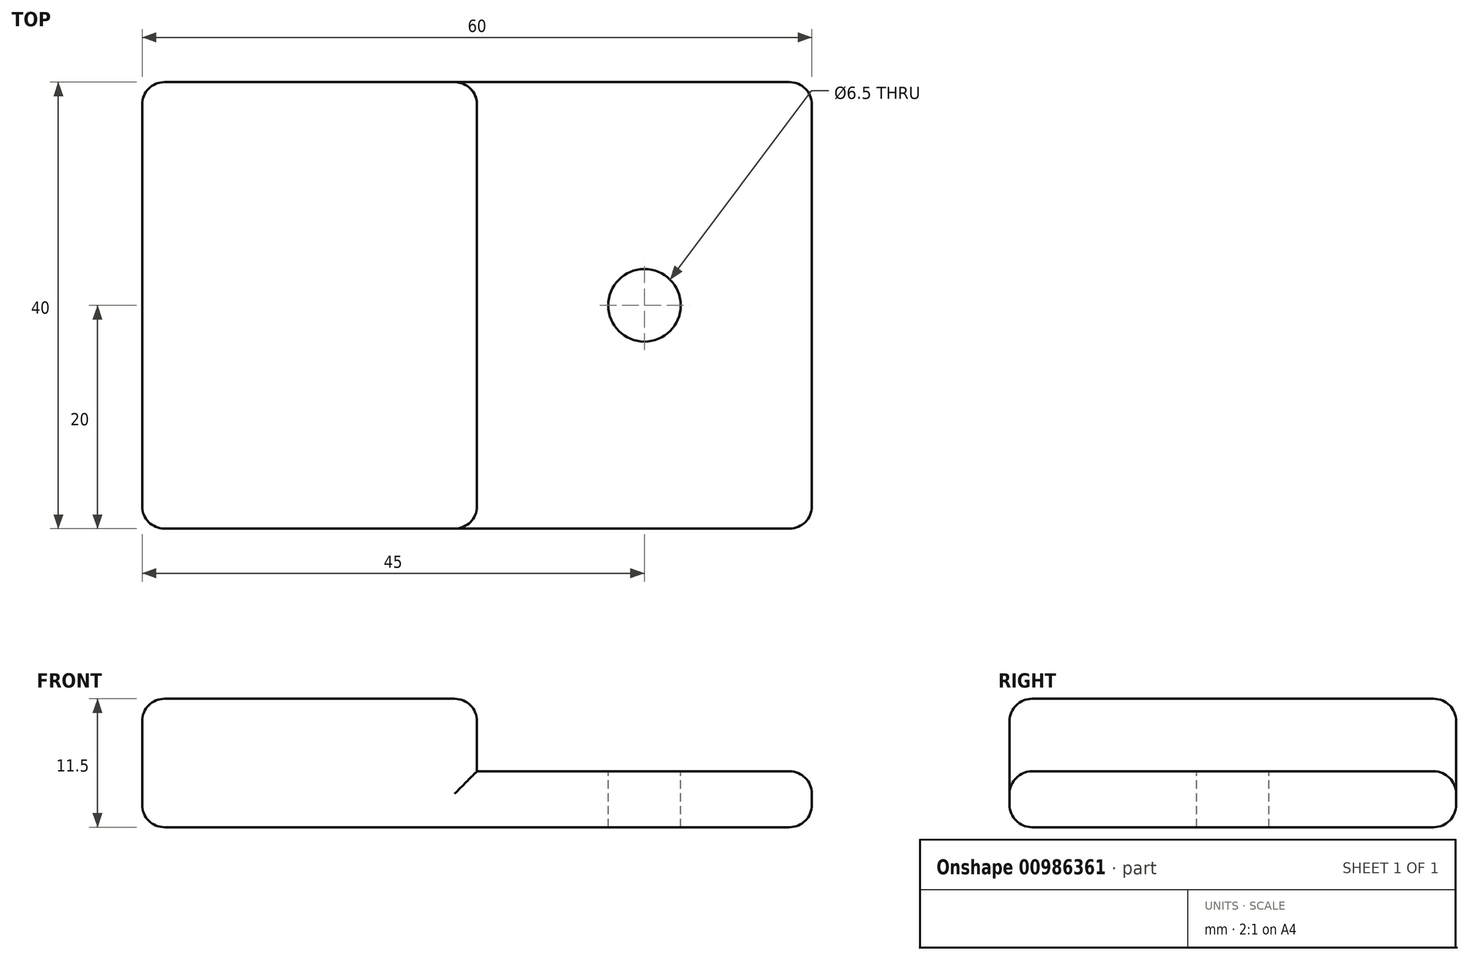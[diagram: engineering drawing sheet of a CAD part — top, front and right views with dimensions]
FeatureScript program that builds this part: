
annotation { "Feature Type Name" : "Feature", "Feature Type Description" : "" }
export const myFeature = defineFeature(function(context is Context, id is Id, definition is map)
    precondition{}
    {
        {
            var Q0;
            Q0=qCreatedBy(makeId("Front.planeOp"),FACE);
            var sketch = newSketch(context, id + "F0", { "sketchPlane" : qUnion([Q0])});
            skLineSegment(sketch, "E0", {"start": v(0, 0) * mm, "end": v(0, 11.5) * mm});
            skLineSegment(sketch, "E1", {"start": v(0, 11.5) * mm, "end": v(30, 11.5) * mm});
            skLineSegment(sketch, "E2", {"start": v(30, 11.5) * mm, "end": v(30, 5) * mm});
            skLineSegment(sketch, "E3", {"start": v(30, 5) * mm, "end": v(60, 5) * mm});
            skLineSegment(sketch, "E4", {"start": v(60, 5) * mm, "end": v(60, 0) * mm});
            skLineSegment(sketch, "E5", {"start": v(60, 0) * mm, "end": v(0, 0) * mm});
            skSolve(sketch);
        }
        {
            var Q0;
            Q0=makeQuery(id+"F0.imprint","IMPRINT",FACE,{"disambiguationData":[TD([[makeQuery(id+"F0.imprint","IMPRINT",EDGE,{"derivedFrom":sQuery(id+"F0.wireOp",EDGE,"E0")}),-1.0]])]});
            extrude(context, id + "F1", {"entities" : qUnion([Q0]), "depth" : 40 * mm, "offsetDistance" : 25 * mm});
        }
        {
            var Q0;
            Q0=makeQuery(id+"F1.opExtrude","SWEPT_FACE",FACE,{"disambiguationData":[OSD([sQuery(id+"F0.wireOp",EDGE,"E3")])]});
            var sketch = newSketch(context, id + "F2", { "sketchPlane" : qUnion([Q0])});
            skLineSegment(sketch, "E6.0", {"start": v(45, -40) * mm, "end": v(45, 0) * mm});
            skLineSegment(sketch, "E7.0", {"start": v(30, -20) * mm, "end": v(60, -20) * mm});
            skCircle(sketch, "E8", {"center": v(45, -20) * mm, "radius": 1.1 * mm});
            skSolve(sketch);
        }
        {
            var Q0;
            Q0=sQuery(id+"F2.wireOp",VERTEX,"E8.center");
            var Q1;
            Q1=makeQuery(id+"F1.opExtrude","SWEPT_BODY",BODY,{"disambiguationData":[OSD([sQuery(id+"F0.wireOp",EDGE,"E0"),sQuery(id+"F0.wireOp",EDGE,"E1"),sQuery(id+"F0.wireOp",EDGE,"E2"),sQuery(id+"F0.wireOp",EDGE,"E3"),sQuery(id+"F0.wireOp",EDGE,"E4"),sQuery(id+"F0.wireOp",EDGE,"E5")])]});
            hole(context, id + "F3", {"style" : HoleStyle.SIMPLE, "endStyle" : HoleEndStyle.BLIND, "holeDiameter" : 6.5 * mm, "majorDiameter" : 5 * mm, "holeDepth" : 30 * mm, "isTappedThrough" : true, "tappedDepth" : 12 * mm, "tapClearance" : 3, "locations" : qUnion([Q0]), "scope" : qUnion([Q1])});
        }
        {
            var Q0;
            Q0=makeQuery(id+"F1.opExtrude","SWEPT_EDGE",EDGE,{"disambiguationData":[OSD([sQuery(id+"F0.wireOp",EDGE,"E0"),sQuery(id+"F0.wireOp",EDGE,"E1")])]});
            var Q1;
            Q1=makeQuery(id+"F1.opExtrude","CAP_EDGE",EDGE,{"disambiguationData":[OSD([sQuery(id+"F0.wireOp",EDGE,"E1")])],"isStart":false});
            var Q2;
            Q2=makeQuery(id+"F1.opExtrude","SWEPT_EDGE",EDGE,{"disambiguationData":[OSD([sQuery(id+"F0.wireOp",EDGE,"E1"),sQuery(id+"F0.wireOp",EDGE,"E2")])]});
            var Q3;
            Q3=makeQuery(id+"F1.opExtrude","CAP_EDGE",EDGE,{"disambiguationData":[OSD([sQuery(id+"F0.wireOp",EDGE,"E1")])],"isStart":true});
            var Q4;
            Q4=makeQuery(id+"F1.opExtrude","CAP_EDGE",EDGE,{"disambiguationData":[OSD([sQuery(id+"F0.wireOp",EDGE,"E0")])],"isStart":true});
            var Q5;
            Q5=makeQuery(id+"F1.opExtrude","CAP_EDGE",EDGE,{"disambiguationData":[OSD([sQuery(id+"F0.wireOp",EDGE,"E0")])],"isStart":false});
            var Q6;
            Q6=makeQuery(id+"F1.opExtrude","CAP_EDGE",EDGE,{"disambiguationData":[OSD([sQuery(id+"F0.wireOp",EDGE,"E2")])],"isStart":false});
            var Q7;
            Q7=makeQuery(id+"F1.opExtrude","CAP_EDGE",EDGE,{"disambiguationData":[OSD([sQuery(id+"F0.wireOp",EDGE,"E2")])],"isStart":true});
            var Q8;
            Q8=makeQuery(id+"F1.opExtrude","CAP_EDGE",EDGE,{"disambiguationData":[OSD([sQuery(id+"F0.wireOp",EDGE,"E3")])],"isStart":false});
            var Q9;
            Q9=makeQuery(id+"F1.opExtrude","SWEPT_EDGE",EDGE,{"disambiguationData":[OSD([sQuery(id+"F0.wireOp",EDGE,"E3"),sQuery(id+"F0.wireOp",EDGE,"E4")])]});
            var Q10;
            Q10=makeQuery(id+"F1.opExtrude","CAP_EDGE",EDGE,{"disambiguationData":[OSD([sQuery(id+"F0.wireOp",EDGE,"E3")])],"isStart":true});
            var Q11;
            Q11=makeQuery(id+"F1.opExtrude","CAP_EDGE",EDGE,{"disambiguationData":[OSD([sQuery(id+"F0.wireOp",EDGE,"E4")])],"isStart":false});
            var Q12;
            Q12=makeQuery(id+"F1.opExtrude","CAP_EDGE",EDGE,{"disambiguationData":[OSD([sQuery(id+"F0.wireOp",EDGE,"E4")])],"isStart":true});
            var Q13;
            Q13=makeQuery(id+"F1.opExtrude","CAP_EDGE",EDGE,{"disambiguationData":[OSD([sQuery(id+"F0.wireOp",EDGE,"E5")])],"isStart":false});
            var Q14;
            Q14=makeQuery(id+"F1.opExtrude","SWEPT_EDGE",EDGE,{"disambiguationData":[OSD([sQuery(id+"F0.wireOp",EDGE,"E0"),sQuery(id+"F0.wireOp",EDGE,"E5")])]});
            var Q15;
            Q15=makeQuery(id+"F1.opExtrude","CAP_EDGE",EDGE,{"disambiguationData":[OSD([sQuery(id+"F0.wireOp",EDGE,"E5")])],"isStart":true});
            var Q16;
            Q16=makeQuery(id+"F1.opExtrude","SWEPT_EDGE",EDGE,{"disambiguationData":[OSD([sQuery(id+"F0.wireOp",EDGE,"E4"),sQuery(id+"F0.wireOp",EDGE,"E5")])]});
            fillet(context, id + "F4", {"entities" : qUnion([Q0, Q1, Q2, Q3, Q4, Q5, Q6, Q7, Q8, Q9, Q10, Q11, Q12, Q13, Q14, Q15, Q16]), "radius" : 2 * mm, "tangentPropagation" : true, "allowEdgeOverflow" : false});
        }
    });
